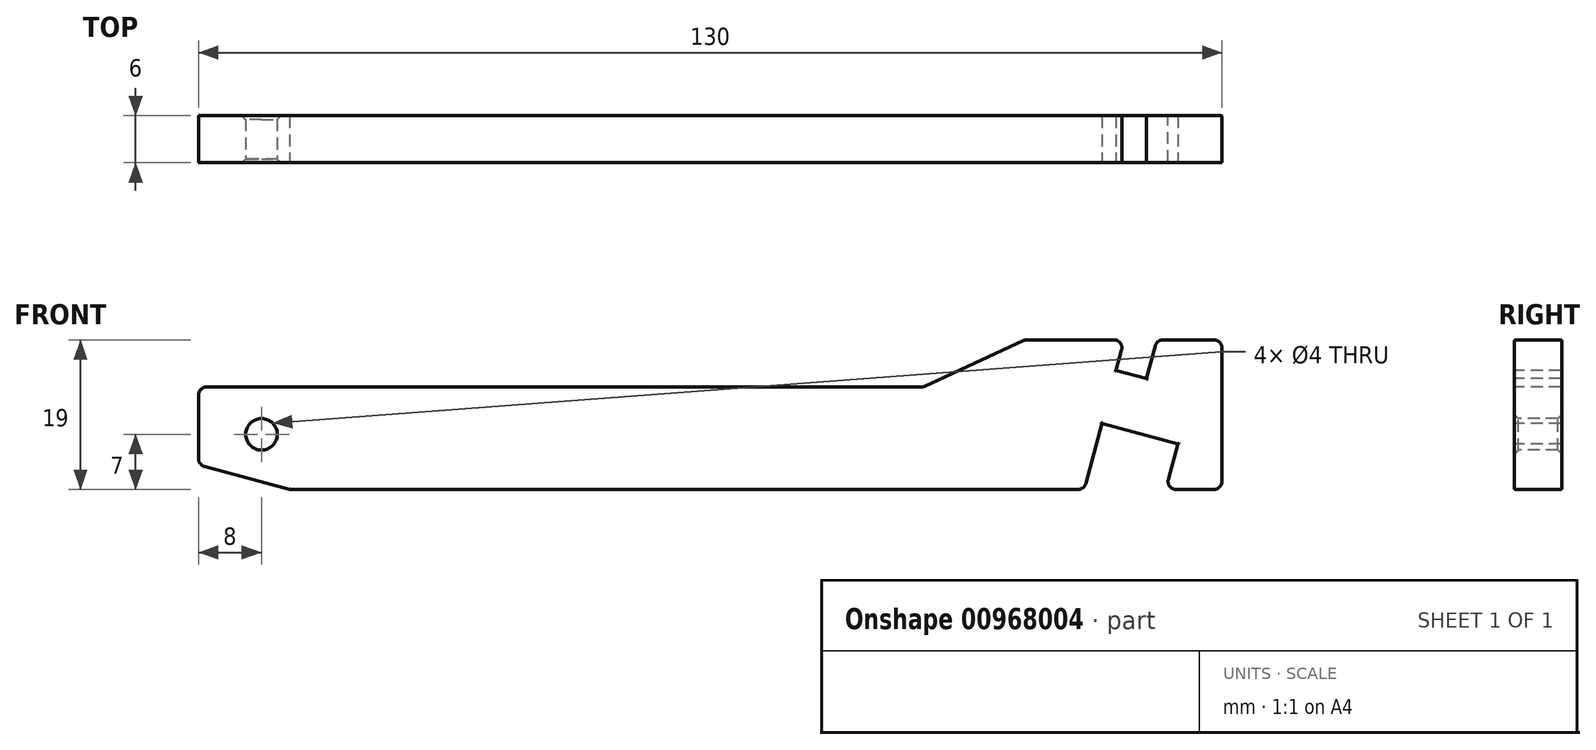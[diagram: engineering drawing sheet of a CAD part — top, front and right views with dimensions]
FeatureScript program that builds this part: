
annotation { "Feature Type Name" : "Feature", "Feature Type Description" : "" }
export const myFeature = defineFeature(function(context is Context, id is Id, definition is map)
    precondition{}
    {
        {
            var Q0;
            Q0=qCreatedBy(makeId("Front.planeOp"),FACE);
            var sketch = newSketch(context, id + "F0", { "sketchPlane" : qUnion([Q0])});
            skLineSegment(sketch, "E0", {"start": v(0, 3.1) * mm, "end": v(0, 13) * mm});
            skLineSegment(sketch, "E1", {"start": v(0, 13) * mm, "end": v(92, 13) * mm});
            skLineSegment(sketch, "E2", {"start": v(92, 13) * mm, "end": v(105, 19) * mm});
            skLineSegment(sketch, "E3", {"start": v(105, 19) * mm, "end": v(117.6, 19) * mm});
            skLineSegment(sketch, "E4", {"start": v(117.6, 19) * mm, "end": v(116.56, 15.14) * mm});
            skLineSegment(sketch, "E5", {"start": v(116.56, 15.14) * mm, "end": v(120.42, 14.1) * mm});
            skLineSegment(sketch, "E6", {"start": v(120.42, 14.1) * mm, "end": v(121.73, 19) * mm});
            skLineSegment(sketch, "E7", {"start": v(121.73, 19) * mm, "end": v(130, 19) * mm});
            skLineSegment(sketch, "E8", {"start": v(130, 19) * mm, "end": v(130, 0) * mm});
            skLineSegment(sketch, "E9.trimOffspring", {"start": v(130, 0) * mm, "end": v(122.85, 0) * mm});
            skLineSegment(sketch, "E10", {"start": v(114.75, 8.38) * mm, "end": v(112.5, 0) * mm});
            skLineSegment(sketch, "E11", {"start": v(114.75, 8.38) * mm, "end": v(124.4, 5.8) * mm});
            skLineSegment(sketch, "E12", {"start": v(124.4, 5.8) * mm, "end": v(122.85, 0) * mm});
            skLineSegment(sketch, "E13.trimOffspring", {"start": v(112.5, 0) * mm, "end": v(11.6, 0) * mm});
            skLineSegment(sketch, "E14", {"start": v(11.6, 0) * mm, "end": v(0, 3.1) * mm});
            skPoint(sketch, "E15.orphan", {"position": v(0, 0) * mm});
            skCircle(sketch, "E16", {"center": v(8, 7) * mm, "radius": 2 * mm});
            skSolve(sketch);
        }
        {
            var Q0;
            Q0=makeQuery(id+"F0.imprint","IMPRINT",FACE,{"disambiguationData":[TD([[makeQuery(id+"F0.imprint","IMPRINT",EDGE,{"derivedFrom":sQuery(id+"F0.wireOp",EDGE,"E0")}),-1.0]])]});
            extrude(context, id + "F1", {"entities" : qUnion([Q0]), "oppositeDirection" : true, "depth" : 6 * mm, "offsetDistance" : 25 * mm});
        }
        {
            var Q0;
            Q0=makeQuery(id+"F1.opExtrude","SWEPT_EDGE",EDGE,{"disambiguationData":[OSD([sQuery(id+"F0.wireOp",EDGE,"E7"),sQuery(id+"F0.wireOp",EDGE,"E8")])]});
            var Q1;
            Q1=makeQuery(id+"F1.opExtrude","SWEPT_EDGE",EDGE,{"disambiguationData":[OSD([sQuery(id+"F0.wireOp",EDGE,"E8"),sQuery(id+"F0.wireOp",EDGE,"E9.trimOffspring")])]});
            var Q2;
            Q2=makeQuery(id+"F1.opExtrude","SWEPT_EDGE",EDGE,{"disambiguationData":[OSD([sQuery(id+"F0.wireOp",EDGE,"E0"),sQuery(id+"F0.wireOp",EDGE,"E1")])]});
            var Q3;
            Q3=makeQuery(id+"F1.opExtrude","SWEPT_EDGE",EDGE,{"disambiguationData":[OSD([sQuery(id+"F0.wireOp",EDGE,"E1"),sQuery(id+"F0.wireOp",EDGE,"E2")])]});
            var Q4;
            Q4=makeQuery(id+"F1.opExtrude","SWEPT_EDGE",EDGE,{"disambiguationData":[OSD([sQuery(id+"F0.wireOp",EDGE,"E2"),sQuery(id+"F0.wireOp",EDGE,"E3")])]});
            var Q5;
            Q5=makeQuery(id+"F1.opExtrude","SWEPT_EDGE",EDGE,{"disambiguationData":[OSD([sQuery(id+"F0.wireOp",EDGE,"E6"),sQuery(id+"F0.wireOp",EDGE,"E7")])]});
            var Q6;
            Q6=makeQuery(id+"F1.opExtrude","SWEPT_EDGE",EDGE,{"disambiguationData":[OSD([sQuery(id+"F0.wireOp",EDGE,"E9.trimOffspring"),sQuery(id+"F0.wireOp",EDGE,"E12")])]});
            var Q7;
            Q7=makeQuery(id+"F1.opExtrude","SWEPT_EDGE",EDGE,{"disambiguationData":[OSD([sQuery(id+"F0.wireOp",EDGE,"E3"),sQuery(id+"F0.wireOp",EDGE,"E4")])]});
            var Q8;
            Q8=makeQuery(id+"F1.opExtrude","SWEPT_EDGE",EDGE,{"disambiguationData":[OSD([sQuery(id+"F0.wireOp",EDGE,"E10"),sQuery(id+"F0.wireOp",EDGE,"E13.trimOffspring")])]});
            var Q9;
            Q9=makeQuery(id+"F1.opExtrude","SWEPT_EDGE",EDGE,{"disambiguationData":[OSD([sQuery(id+"F0.wireOp",EDGE,"E0"),sQuery(id+"F0.wireOp",EDGE,"E14")])]});
            fillet(context, id + "F2", {"entities" : qUnion([Q0, Q1, Q2, Q3, Q4, Q5, Q6, Q7, Q8, Q9]), "radius" : 1 * mm, "tangentPropagation" : true, "allowEdgeOverflow" : false});
        }
        {
            var Q0;
            Q0=makeQuery(id+"F1.opExtrude","CAP_EDGE",EDGE,{"disambiguationData":[OSD([sQuery(id+"F0.wireOp",EDGE,"E16")])],"isStart":false});
            var Q1;
            Q1=makeQuery(id+"F1.opExtrude","CAP_EDGE",EDGE,{"disambiguationData":[OSD([sQuery(id+"F0.wireOp",EDGE,"E16")])],"isStart":true});
            chamfer(context, id + "F3", {"entities" : qUnion([Q0, Q1]), "width" : .5 * mm, "tangentPropagation" : true});
        }
        {
            var Q0;
            Q0=makeQuery(id+"F1.opExtrude","CAP_FACE",FACE,{"disambiguationData":[OSD([sQuery(id+"F0.wireOp",EDGE,"E0"),sQuery(id+"F0.wireOp",EDGE,"E1"),sQuery(id+"F0.wireOp",EDGE,"E2"),sQuery(id+"F0.wireOp",EDGE,"E3"),sQuery(id+"F0.wireOp",EDGE,"E4"),sQuery(id+"F0.wireOp",EDGE,"E5"),sQuery(id+"F0.wireOp",EDGE,"E6"),sQuery(id+"F0.wireOp",EDGE,"E7"),sQuery(id+"F0.wireOp",EDGE,"E8"),sQuery(id+"F0.wireOp",EDGE,"E9.trimOffspring"),sQuery(id+"F0.wireOp",EDGE,"E10"),sQuery(id+"F0.wireOp",EDGE,"E11"),sQuery(id+"F0.wireOp",EDGE,"E12"),sQuery(id+"F0.wireOp",EDGE,"E13.trimOffspring"),sQuery(id+"F0.wireOp",EDGE,"E14"),sQuery(id+"F0.wireOp",EDGE,"E16")])],"isStart":true});
            var Q1;
            Q1=makeQuery(id+"F1.opExtrude","CAP_FACE",FACE,{"disambiguationData":[OSD([sQuery(id+"F0.wireOp",EDGE,"E0"),sQuery(id+"F0.wireOp",EDGE,"E1"),sQuery(id+"F0.wireOp",EDGE,"E2"),sQuery(id+"F0.wireOp",EDGE,"E3"),sQuery(id+"F0.wireOp",EDGE,"E4"),sQuery(id+"F0.wireOp",EDGE,"E5"),sQuery(id+"F0.wireOp",EDGE,"E6"),sQuery(id+"F0.wireOp",EDGE,"E7"),sQuery(id+"F0.wireOp",EDGE,"E8"),sQuery(id+"F0.wireOp",EDGE,"E9.trimOffspring"),sQuery(id+"F0.wireOp",EDGE,"E10"),sQuery(id+"F0.wireOp",EDGE,"E11"),sQuery(id+"F0.wireOp",EDGE,"E12"),sQuery(id+"F0.wireOp",EDGE,"E13.trimOffspring"),sQuery(id+"F0.wireOp",EDGE,"E14"),sQuery(id+"F0.wireOp",EDGE,"E16")])],"isStart":false});
            fillet(context, id + "F4", {"entities" : qUnion([Q0, Q1]), "radius" : .125 * mm, "tangentPropagation" : true, "allowEdgeOverflow" : false});
        }
    });
